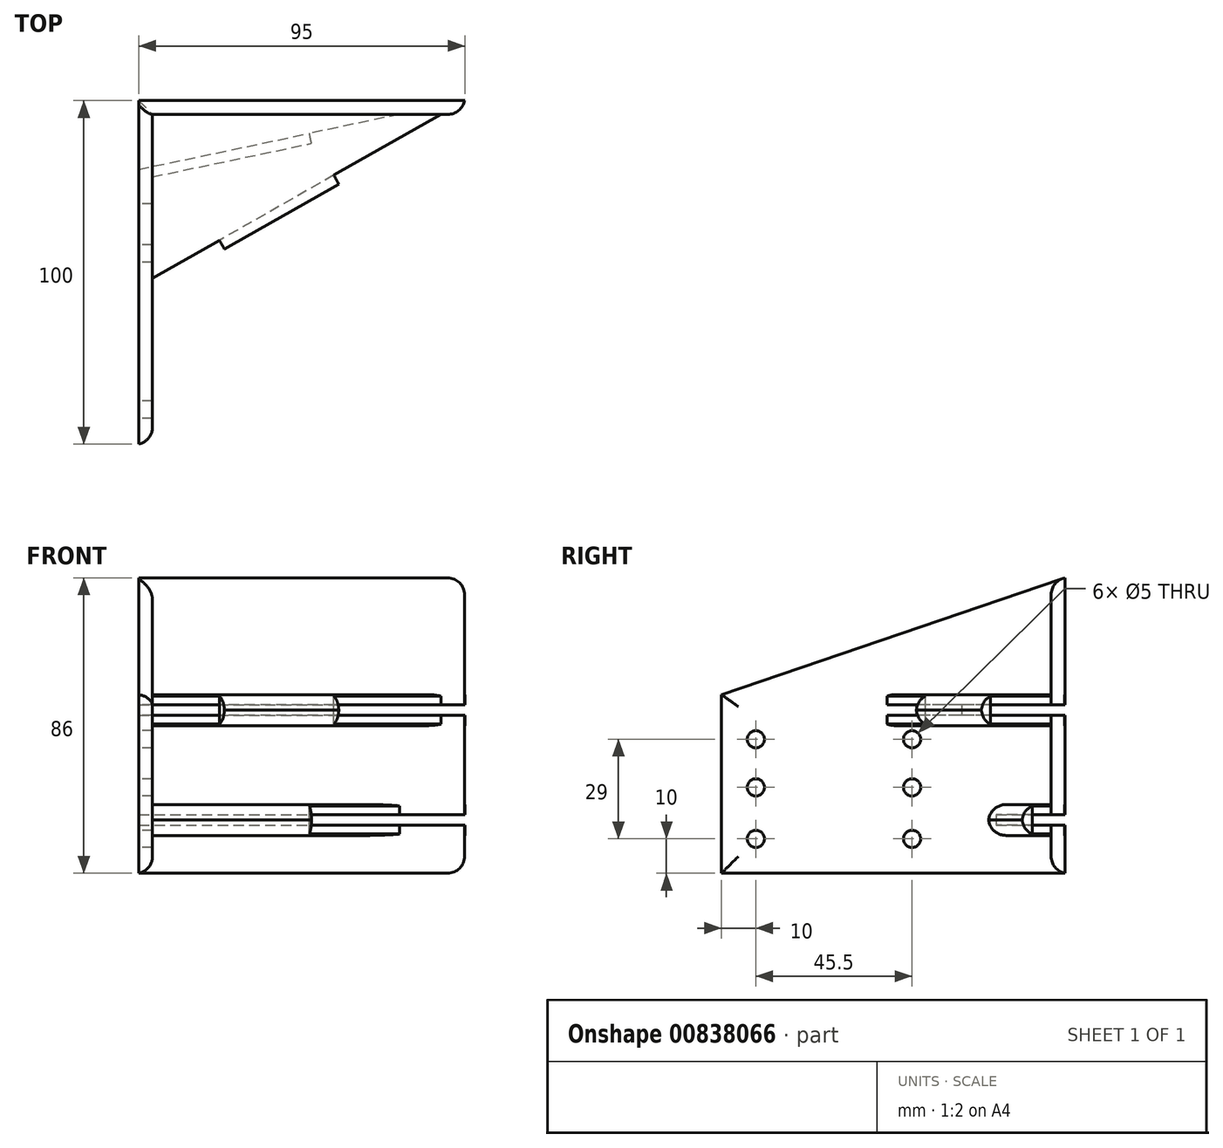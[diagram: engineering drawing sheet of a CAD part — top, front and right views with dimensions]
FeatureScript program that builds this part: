
annotation { "Feature Type Name" : "Feature", "Feature Type Description" : "" }
export const myFeature = defineFeature(function(context is Context, id is Id, definition is map)
    precondition{}
    {
        {
            var Q0;
            Q0=qCreatedBy(makeId("Front.planeOp"),FACE);
            var sketch = newSketch(context, id + "F0", { "sketchPlane" : qUnion([Q0])});
            skLineSegment(sketch, "E0.bottom", {"start": v(0, 0) * mm, "end": v(-95, 0) * mm});
            skLineSegment(sketch, "E0.top", {"start": v(0, 86) * mm, "end": v(-95, 86) * mm});
            skLineSegment(sketch, "E0.left", {"start": v(0, 0) * mm, "end": v(0, 86) * mm});
            skLineSegment(sketch, "E0.right", {"start": v(-95, 0) * mm, "end": v(-95, 86) * mm});
            skSolve(sketch);
        }
        {
            var Q0;
            Q0 = qSketchRegion(id + "F0", true);
            extrude(context, id + "F1", {"entities" : qUnion([Q0]), "depth" : 4 * mm, "offsetDistance" : 25 * mm});
        }
        {
            var Q0;
            Q0=makeQuery(id+"F1.opExtrude","CAP_EDGE",EDGE,{"disambiguationData":[OSD([sQuery(id+"F0.wireOp",EDGE,"E0.top")])],"isStart":false});
            var Q1;
            Q1=makeQuery(id+"F1.opExtrude","CAP_EDGE",EDGE,{"disambiguationData":[OSD([sQuery(id+"F0.wireOp",EDGE,"E0.bottom")])],"isStart":false});
            fillet(context, id + "F2", {"entities" : qUnion([Q0, Q1]), "radius" : 5 * mm, "tangentPropagation" : true, "allowEdgeOverflow" : false});
        }
        {
            var Q0;
            Q0=makeQuery(id+"F1.opExtrude","CAP_EDGE",EDGE,{"disambiguationData":[OSD([sQuery(id+"F0.wireOp",EDGE,"E0.left")])],"isStart":false});
            fillet(context, id + "F3", {"entities" : qUnion([Q0]), "radius" : 5 * mm, "tangentPropagation" : true, "allowEdgeOverflow" : false});
        }
        {
            var Q0;
            Q0=qCreatedBy(makeId("Right.planeOp"),FACE);
            cPlane(context, id + "F4", {"entities" : qUnion([Q0]), "cplaneType" : CPlaneType.OFFSET, "offset" : 95 * mm, "oppositeDirection" : true, "width" : 150 * mm, "height" : 150 * mm});
        }
        {
            var Q0;
            Q0=qCreatedBy(id+"F4.planeOp",FACE);
            var sketch = newSketch(context, id + "F5", { "sketchPlane" : qUnion([Q0])});
            skLineSegment(sketch, "E1.bottom", {"start": v(-100, 52) * mm, "end": v(0, 52) * mm});
            skLineSegment(sketch, "E1.top", {"start": v(-100, 0) * mm, "end": v(0, 0) * mm});
            skLineSegment(sketch, "E1.left", {"start": v(-100, 52) * mm, "end": v(-100, 0) * mm});
            skLineSegment(sketch, "E1.right", {"start": v(0, 52) * mm, "end": v(0, 0) * mm});
            skSolve(sketch);
        }
        {
            var Q0;
            Q0 = qSketchRegion(id + "F5", true);
            extrude(context, id + "F6", {"entities" : qUnion([Q0]), "operationType" : NewBodyOperationType.ADD, "depth" : 4 * mm, "offsetDistance" : 25 * mm});
        }
        {
            var Q0;
            Q0=makeQuery(id+"F6.opExtrude","CAP_EDGE",EDGE,{"disambiguationData":[OSD([sQuery(id+"F5.wireOp",EDGE,"E1.left")])],"isStart":false});
            var Q1;
            Q1=makeQuery(id+"F6.opExtrude","CAP_EDGE",EDGE,{"disambiguationData":[OSD([sQuery(id+"F5.wireOp",EDGE,"E1.top")])],"isStart":false});
            fillet(context, id + "F7", {"entities" : qUnion([Q0, Q1]), "radius" : 5 * mm, "tangentPropagation" : true, "allowEdgeOverflow" : false});
        }
        {
            var Q0;
            Q0=qCreatedBy(makeId("Top.planeOp"),FACE);
            cPlane(context, id + "F8", {"entities" : qUnion([Q0]), "cplaneType" : CPlaneType.OFFSET, "offset" : 46 * mm, "width" : 150 * mm, "height" : 150 * mm});
        }
        {
            var Q0;
            Q0=qCreatedBy(id+"F8.planeOp",FACE);
            var sketch = newSketch(context, id + "F9", { "sketchPlane" : qUnion([Q0])});
            skLineSegment(sketch, "E2", {"start": v(-95, -54) * mm, "end": v(-95, 0) * mm});
            skLineSegment(sketch, "E3", {"start": v(-95, 0) * mm, "end": v(0, 0) * mm});
            skLineSegment(sketch, "E4", {"start": v(0, 0) * mm, "end": v(-95, -54) * mm});
            skSolve(sketch);
        }
        {
            var Q0;
            Q0 = qSketchRegion(id + "F9", true);
            extrude(context, id + "F10", {"entities" : qUnion([Q0]), "operationType" : NewBodyOperationType.ADD, "oppositeDirection" : true, "depth" : 3 * mm, "offsetDistance" : 25 * mm});
        }
        {
            var Q0;
            Q0=qCreatedBy(makeId("Top.planeOp"),FACE);
            cPlane(context, id + "F11", {"entities" : qUnion([Q0]), "cplaneType" : CPlaneType.OFFSET, "offset" : 49 * mm, "width" : 150 * mm, "height" : 150 * mm});
        }
        {
            var Q0;
            Q0=qCreatedBy(id+"F11.planeOp",FACE);
            var sketch = newSketch(context, id + "F12", { "sketchPlane" : qUnion([Q0])});
            skLineSegment(sketch, "E5", {"start": v(-95, -54) * mm, "end": v(-95, 0) * mm});
            skLineSegment(sketch, "E6", {"start": v(-95, 0) * mm, "end": v(0, 0) * mm});
            skLineSegment(sketch, "E7", {"start": v(0, 0) * mm, "end": v(-95, -54) * mm});
            skSolve(sketch);
        }
        {
            var Q0;
            Q0 = qSketchRegion(id + "F12", true);
            extrude(context, id + "F13", {"entities" : qUnion([Q0]), "operationType" : NewBodyOperationType.ADD, "depth" : 3 * mm, "offsetDistance" : 25 * mm});
        }
        {
            var Q0;
            Q0=qCreatedBy(id+"F8.planeOp",FACE);
            var sketch = newSketch(context, id + "F14", { "sketchPlane" : qUnion([Q0])});
            skLineSegment(sketch, "E8.bottom", {"start": v(0, 0) * mm, "end": v(-95, 0) * mm});
            skLineSegment(sketch, "E8.top", {"start": v(0, -30) * mm, "end": v(-95, -30) * mm});
            skLineSegment(sketch, "E8.left", {"start": v(0, 0) * mm, "end": v(0, -30) * mm});
            skLineSegment(sketch, "E8.right", {"start": v(-95, 0) * mm, "end": v(-95, -30) * mm});
            skSolve(sketch);
        }
        {
            var Q0;
            Q0 = qSketchRegion(id + "F14", true);
            extrude(context, id + "F15", {"entities" : qUnion([Q0]), "operationType" : NewBodyOperationType.REMOVE, "depth" : 3 * mm, "offsetDistance" : 25 * mm});
        }
        {
            var Q0;
            Q0=qCreatedBy(id+"F4.planeOp",FACE);
            var sketch = newSketch(context, id + "F16", { "sketchPlane" : qUnion([Q0])});
            skLineSegment(sketch, "E9", {"start": v(0, 52) * mm, "end": v(-100, 52) * mm});
            skLineSegment(sketch, "E10", {"start": v(-100, 52) * mm, "end": v(0, 86) * mm});
            skLineSegment(sketch, "E11", {"start": v(0, 86) * mm, "end": v(0, 52) * mm});
            skSolve(sketch);
        }
        {
            var Q0;
            Q0 = qSketchRegion(id + "F16", true);
            extrude(context, id + "F17", {"entities" : qUnion([Q0]), "operationType" : NewBodyOperationType.ADD, "depth" : 4 * mm, "offsetDistance" : 25 * mm});
        }
        {
            var Q0;
            Q0=makeQuery(id+"F17.opExtrude","CAP_EDGE",EDGE,{"disambiguationData":[OSD([sQuery(id+"F16.wireOp",EDGE,"E10")])],"isStart":false});
            fillet(context, id + "F18", {"entities" : qUnion([Q0]), "radius" : 5 * mm, "tangentPropagation" : true, "allowEdgeOverflow" : false});
        }
        {
            var Q0;
            Q0=qCreatedBy(makeId("Top.planeOp"),FACE);
            cPlane(context, id + "F19", {"entities" : qUnion([Q0]), "cplaneType" : CPlaneType.OFFSET, "offset" : 14 * mm, "width" : 150 * mm, "height" : 150 * mm});
        }
        {
            var Q0;
            Q0=qCreatedBy(id+"F19.planeOp",FACE);
            var sketch = newSketch(context, id + "F20", { "sketchPlane" : qUnion([Q0])});
            skLineSegment(sketch, "E12", {"start": v(-95, -20) * mm, "end": v(-95, 0) * mm});
            skLineSegment(sketch, "E13", {"start": v(-95, 0) * mm, "end": v(0, 0) * mm});
            skLineSegment(sketch, "E14", {"start": v(0, 0) * mm, "end": v(-95, -20) * mm});
            skSolve(sketch);
        }
        {
            var Q0;
            Q0 = qSketchRegion(id + "F20", true);
            extrude(context, id + "F21", {"entities" : qUnion([Q0]), "operationType" : NewBodyOperationType.ADD, "oppositeDirection" : true, "depth" : 3 * mm, "offsetDistance" : 25 * mm});
        }
        {
            var Q0;
            Q0=qCreatedBy(makeId("Top.planeOp"),FACE);
            cPlane(context, id + "F22", {"entities" : qUnion([Q0]), "cplaneType" : CPlaneType.OFFSET, "offset" : 17 * mm, "width" : 150 * mm, "height" : 150 * mm});
        }
        {
            var Q0;
            Q0=qCreatedBy(id+"F22.planeOp",FACE);
            var sketch = newSketch(context, id + "F23", { "sketchPlane" : qUnion([Q0])});
            skLineSegment(sketch, "E15", {"start": v(-95, -20) * mm, "end": v(-95, 0) * mm});
            skLineSegment(sketch, "E16", {"start": v(-95, 0) * mm, "end": v(0, 0) * mm});
            skLineSegment(sketch, "E17", {"start": v(0, 0) * mm, "end": v(-95, -20) * mm});
            skSolve(sketch);
        }
        {
            var Q0;
            Q0 = qSketchRegion(id + "F23", true);
            extrude(context, id + "F24", {"entities" : qUnion([Q0]), "operationType" : NewBodyOperationType.ADD, "depth" : 3 * mm, "offsetDistance" : 25 * mm});
        }
        {
            var Q0;
            Q0=qCreatedBy(id+"F19.planeOp",FACE);
            var sketch = newSketch(context, id + "F25", { "sketchPlane" : qUnion([Q0])});
            skLineSegment(sketch, "E18.bottom", {"start": v(0, 0) * mm, "end": v(-95, 0) * mm});
            skLineSegment(sketch, "E18.top", {"start": v(0, -20) * mm, "end": v(-95, -20) * mm});
            skLineSegment(sketch, "E18.left", {"start": v(0, 0) * mm, "end": v(0, -20) * mm});
            skLineSegment(sketch, "E18.right", {"start": v(-95, 0) * mm, "end": v(-95, -20) * mm});
            skSolve(sketch);
        }
        {
            var Q0;
            Q0 = qSketchRegion(id + "F25", true);
            extrude(context, id + "F26", {"entities" : qUnion([Q0]), "operationType" : NewBodyOperationType.REMOVE, "depth" : 3 * mm, "offsetDistance" : 25 * mm});
        }
        {
            var Q0;
            {var subQ0=sQuery(id+"F20.wireOp",EDGE,"E14");Q0=makeQuery(id+"F21.boolean.opBoolean","SPLIT",FACE,{"disambiguationData":[TD([makeQuery(id+"F1.opExtrude","CAP_FACE",FACE,{"disambiguationData":[OSD([sQuery(id+"F0.wireOp",EDGE,"E0.bottom"),sQuery(id+"F0.wireOp",EDGE,"E0.top"),sQuery(id+"F0.wireOp",EDGE,"E0.left"),sQuery(id+"F0.wireOp",EDGE,"E0.right")])],"isStart":false})])],"derivedFrom":makeQuery(id+"F21.opExtrude","SWEPT_FACE",FACE,{"disambiguationData":[OSD([subQ0])]})});}
            var sketch = newSketch(context, id + "F27", { "sketchPlane" : qUnion([Q0])});
            skPoint(sketch, "E19.oppositeSnap0", {"position": v(-46.28, 11) * mm});
            skLineSegment(sketch, "E19.bottom", {"start": v(-97.08, 11) * mm, "end": v(-46.28, 11) * mm});
            skLineSegment(sketch, "E19.top", {"start": v(-97.08, 20) * mm, "end": v(-46.28, 20) * mm});
            skLineSegment(sketch, "E19.left", {"start": v(-97.08, 11) * mm, "end": v(-97.08, 20) * mm});
            skLineSegment(sketch, "E19.right", {"start": v(-46.28, 11) * mm, "end": v(-46.28, 20) * mm});
            skSolve(sketch);
        }
        {
            var Q0;
            Q0 = qSketchRegion(id + "F27", true);
            extrude(context, id + "F28", {"entities" : qUnion([Q0]), "operationType" : NewBodyOperationType.ADD, "depth" : 3 * mm, "offsetDistance" : 25 * mm});
        }
        {
            var Q0;
            Q0=makeQuery(id+"F28.opExtrude","CAP_EDGE",EDGE,{"disambiguationData":[OSD([sQuery(id+"F27.wireOp",EDGE,"E19.top")])],"isStart":false});
            var Q1;
            Q1=makeQuery(id+"F28.opExtrude","CAP_EDGE",EDGE,{"disambiguationData":[OSD([sQuery(id+"F27.wireOp",EDGE,"E19.bottom")])],"isStart":false});
            fillet(context, id + "F29", {"entities" : qUnion([Q0, Q1]), "radius" : 5 * mm, "tangentPropagation" : true, "allowEdgeOverflow" : false});
        }
        {
            var Q0;
            Q0=makeQuery(id+"F17.boolean.opBoolean","MERGE",FACE,{"derivedFrom":[makeQuery(id+"F6.boolean.opBoolean","MERGE",FACE,{"derivedFrom":[makeQuery(id+"F1.opExtrude","SWEPT_FACE",FACE,{"disambiguationData":[OSD([sQuery(id+"F0.wireOp",EDGE,"E0.right")])]}),makeQuery(id+"F6.opExtrude","CAP_FACE",FACE,{"disambiguationData":[OSD([sQuery(id+"F5.wireOp",EDGE,"E1.bottom"),sQuery(id+"F5.wireOp",EDGE,"E1.top"),sQuery(id+"F5.wireOp",EDGE,"E1.left"),sQuery(id+"F5.wireOp",EDGE,"E1.right")])],"isStart":true})]}),makeQuery(id+"F17.opExtrude","CAP_FACE",FACE,{"disambiguationData":[OSD([sQuery(id+"F16.wireOp",EDGE,"E9"),sQuery(id+"F16.wireOp",EDGE,"E10"),sQuery(id+"F16.wireOp",EDGE,"E11")])],"isStart":true})]});
            var sketch = newSketch(context, id + "F30", { "sketchPlane" : qUnion([Q0])});
            skLineSegment(sketch, "E20", {"start": v(44.5, 72.99) * mm, "end": v(44.5, -16.8) * mm, "construction": true});
            skLineSegment(sketch, "E21", {"start": v(31, 79.33) * mm, "end": v(31, -4.72) * mm, "construction": true});
            skLineSegment(sketch, "E22", {"start": v(-6.95, 39) * mm, "end": v(72.66, 39) * mm, "construction": true});
            skLineSegment(sketch, "E23", {"start": v(-13.26, 10) * mm, "end": v(83.93, 10) * mm, "construction": true});
            skCircle(sketch, "E24", {"center": v(44.5, 39) * mm, "radius": 2.5 * mm});
            skCircle(sketch, "E25", {"center": v(44.5, 10) * mm, "radius": 2.5 * mm});
            skLineSegment(sketch, "E26", {"start": v(-4.24, 25) * mm, "end": v(74.22, 25) * mm, "construction": true});
            skCircle(sketch, "E27", {"center": v(44.5, 25) * mm, "radius": 2.5 * mm});
            skLineSegment(sketch, "E28", {"start": v(90, -26.23) * mm, "end": v(90, 74.96) * mm, "construction": true});
            skCircle(sketch, "E29", {"center": v(90, 39) * mm, "radius": 2.5 * mm});
            skCircle(sketch, "E30", {"center": v(90, 25) * mm, "radius": 2.5 * mm});
            skCircle(sketch, "E31", {"center": v(90, 10) * mm, "radius": 2.5 * mm});
            skSolve(sketch);
        }
        {
            var Q0;
            Q0 = qSketchRegion(id + "F30", true);
            extrude(context, id + "F31", {"entities" : qUnion([Q0]), "operationType" : NewBodyOperationType.REMOVE, "oppositeDirection" : true, "depth" : 5 * mm, "offsetDistance" : 25 * mm});
        }
        {
            var Q0;
            {var subQ0=sQuery(id+"F9.wireOp",EDGE,"E4");Q0=makeQuery(id+"F10.boolean.opBoolean","SPLIT",FACE,{"disambiguationData":[TD([makeQuery(id+"F1.opExtrude","CAP_FACE",FACE,{"disambiguationData":[OSD([sQuery(id+"F0.wireOp",EDGE,"E0.bottom"),sQuery(id+"F0.wireOp",EDGE,"E0.top"),sQuery(id+"F0.wireOp",EDGE,"E0.left"),sQuery(id+"F0.wireOp",EDGE,"E0.right")])],"isStart":false})])],"derivedFrom":makeQuery(id+"F10.opExtrude","SWEPT_FACE",FACE,{"disambiguationData":[OSD([subQ0])]})});}
            var sketch = newSketch(context, id + "F32", { "sketchPlane" : qUnion([Q0])});
            skLineSegment(sketch, "E32.bottom", {"start": v(-82.25, 43) * mm, "end": v(-43.94, 43) * mm});
            skLineSegment(sketch, "E32.top", {"start": v(-82.25, 52) * mm, "end": v(-43.94, 52) * mm});
            skLineSegment(sketch, "E32.left", {"start": v(-82.25, 43) * mm, "end": v(-82.25, 52) * mm});
            skLineSegment(sketch, "E32.right", {"start": v(-43.94, 43) * mm, "end": v(-43.94, 52) * mm});
            skSolve(sketch);
        }
        {
            var Q0;
            Q0 = qSketchRegion(id + "F32", true);
            extrude(context, id + "F33", {"entities" : qUnion([Q0]), "operationType" : NewBodyOperationType.ADD, "depth" : 3 * mm, "offsetDistance" : 25 * mm});
        }
        {
            var Q0;
            Q0=makeQuery(id+"F33.opExtrude","CAP_EDGE",EDGE,{"disambiguationData":[OSD([sQuery(id+"F32.wireOp",EDGE,"E32.bottom")])],"isStart":false});
            var Q1;
            Q1=makeQuery(id+"F33.opExtrude","CAP_EDGE",EDGE,{"disambiguationData":[OSD([sQuery(id+"F32.wireOp",EDGE,"E32.top")])],"isStart":false});
            fillet(context, id + "F34", {"entities" : qUnion([Q0, Q1]), "radius" : 5 * mm, "tangentPropagation" : true, "allowEdgeOverflow" : false});
        }
    });
